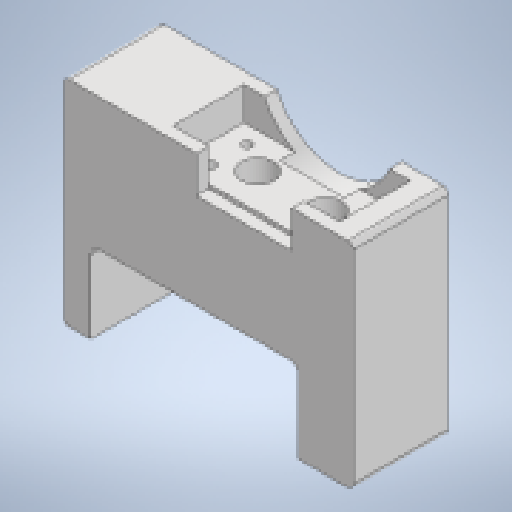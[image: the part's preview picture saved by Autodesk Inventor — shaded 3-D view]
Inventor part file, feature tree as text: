
AUTODESK INVENTOR PART (.ipt)
format: ipt  version: 2023 (Build 270158000, 158)  size: 229,888 bytes
history: native  units: in
note: dims shown in document units (in); Inventor stores cm internally (conversion verified against a paired STEP export)
features: extrude x8, sketch x7, fillet x2
ambient origin geometry x8: Origin, YZ Plane, XZ Plane, XY Plane, X Axis, Y Axis, Z Axis, Center Point
bodies: Solid1 (feature_tree)
feature tree (17):
  sketch  "Sketch1"  dims[d0=0.9843in d1=2.3622in]
  extrude  "Extrusion1"  Depth=0.9843in
  extrude  "Extrusion2"  Depth=0.0197in
  extrude  "Extrusion3"  Depth=0.0197in
  extrude  "Extrusion4"  Depth=1.811in
  extrude  "Extrusion5"  Depth=4.1811in
  extrude  "Extrusion6"  Depth=0.3937in TaperAngle=0.0deg
  fillet  "Fillet1"  Radius=0.3937in
  fillet  "Fillet2"  Radius=3.0in
  extrude  "Extrusion7"  Depth=0.125in
  extrude  "Extrusion8"  Depth=0.7874in
  sketch  "Sketch2"  dims[d2=0.0197in d3=0.0197in]
  sketch  "Sketch3"  dims[d4=0.0197in d5=0.0197in]
  sketch  "Sketch4"  dims[d6=0.1417in d7=1.811in]
  sketch  "Sketch5"  dims[d8=0.5118in d9=4.1811in]
  sketch  "Sketch6"  dims[d10=1.378in d11=0.3937in d12=0.0in]
  sketch  "Sketch7"  dims[d13=1.5118in d14=0.0in d15=0.3937in d16=0.0787in d17=0.0in d18=0.0in d19=0.3937in d20=1.1969in d21=0.0in d22=0.0in d23=3.0in d24=0.125in d25=0.7874in d26=1.1811in d27=0.3937in d28=0.0in d29=0.2362in d30=0.9843in d31=0.3937in d32=0.0in d34=0.4724in d35=0.3937in d36=0.0in d37=0.0787in d38=0.0787in d39=1.374in d40=1.378in d41=2.0812in d42=0.0in d44=0.9843in d45=0.3937in d46=0.3937in d47=0.0in d49=1.5748in d50=1.5748in d51=0.3937in]
